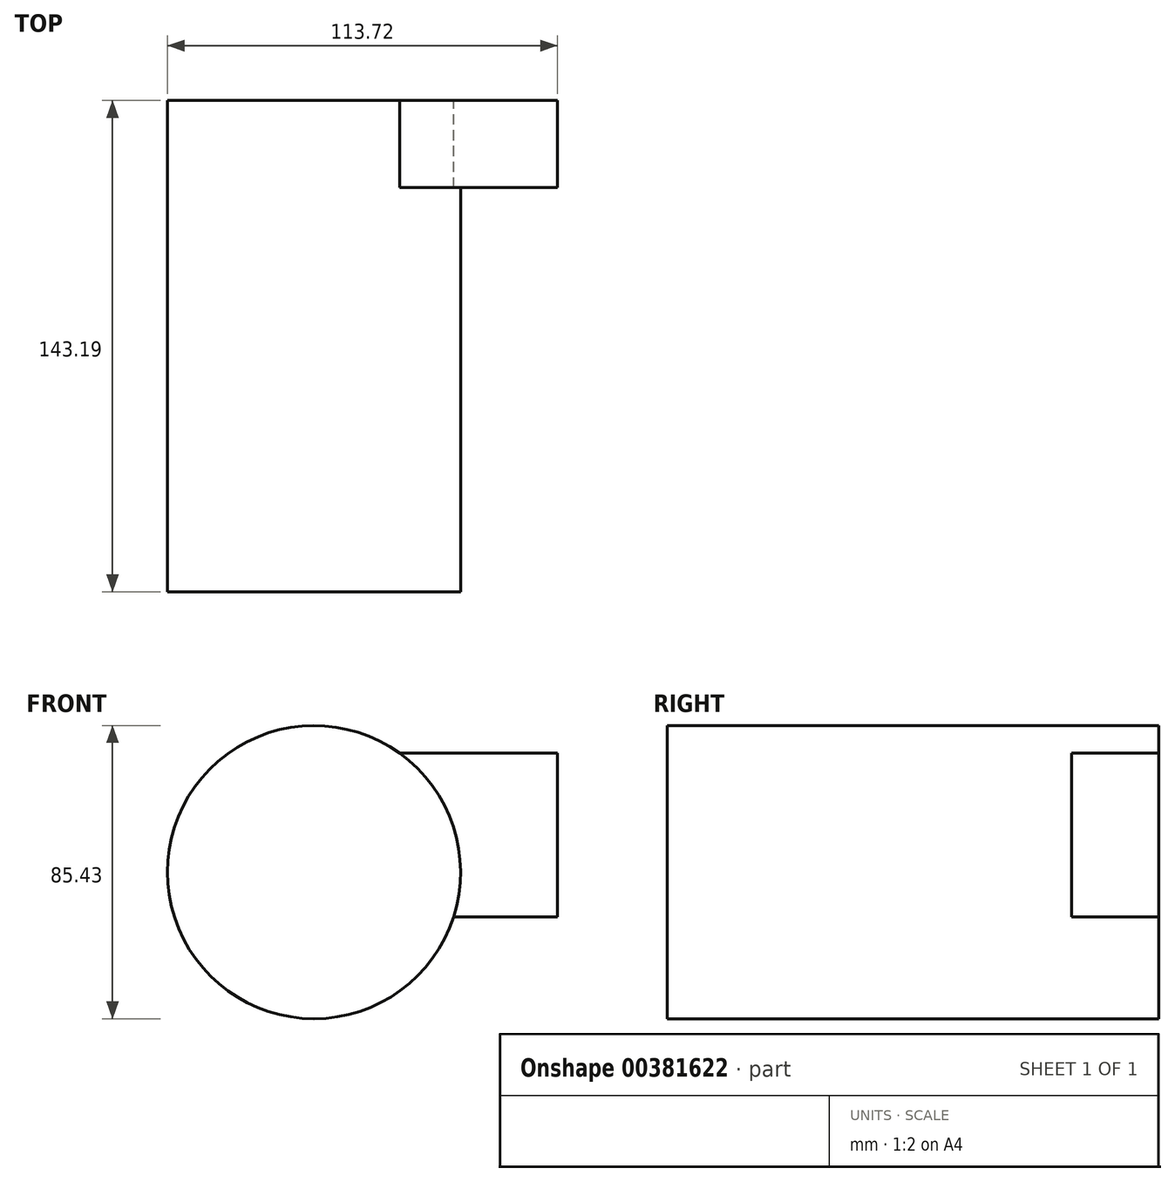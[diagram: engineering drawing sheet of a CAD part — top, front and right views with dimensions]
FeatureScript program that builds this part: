
annotation { "Feature Type Name" : "Feature", "Feature Type Description" : "" }
export const myFeature = defineFeature(function(context is Context, id is Id, definition is map)
    precondition{}
    {
        {
            var Q0;
            Q0=qCreatedBy(makeId("Front.planeOp"),FACE);
            var sketch = newSketch(context, id + "F0", { "sketchPlane" : qUnion([Q0])});
            skCircle(sketch, "E0", {"center": v(6.75, 13.03) * mm, "radius": 42.71 * mm});
            skSolve(sketch);
        }
        {
            var Q0;
            Q0=makeQuery(id+"F0.imprint","IMPRINT",FACE,{"disambiguationData":[TD([[makeQuery(id+"F0.imprint","IMPRINT",EDGE,{"derivedFrom":sQuery(id+"F0.wireOp",EDGE,"E0")}),1.0]])]});
            extrude(context, id + "F1", {"entities" : qUnion([Q0]), "depth" : 67 * mm});
        }
        {
            var Q0;
            Q0=qCreatedBy(makeId("Front.planeOp"),FACE);
            var sketch = newSketch(context, id + "F2", { "sketchPlane" : qUnion([Q0])});
            skLineSegment(sketch, "E1.bottom", {"start": v(52.36, 0) * mm, "end": v(0, 0) * mm});
            skLineSegment(sketch, "E1.top", {"start": v(52.36, 47.73) * mm, "end": v(0, 47.73) * mm});
            skLineSegment(sketch, "E1.left", {"start": v(52.36, 0) * mm, "end": v(52.36, 47.73) * mm});
            skLineSegment(sketch, "E1.right", {"start": v(0, 0) * mm, "end": v(0, 47.73) * mm});
            skSolve(sketch);
        }
        {
            var Q0;
            Q0=makeQuery(id+"F1.opExtrude","CAP_FACE",FACE,{"disambiguationData":[OSD([sQuery(id+"F0.wireOp",EDGE,"E0")])],"isStart":false});
            var Q1;
            Q1=makeQuery(id+"F2.imprint","IMPRINT",FACE,{"disambiguationData":[TD([[makeQuery(id+"F2.imprint","IMPRINT",EDGE,{"derivedFrom":sQuery(id+"F2.wireOp",EDGE,"E1.bottom")}),-1.0]])]});
            extrude(context, id + "F3", {"entities" : qUnion([Q0, Q1]), "operationType" : NewBodyOperationType.ADD, "depth" : 25.4 * mm});
        }
        {
            var Q0;
            Q0=makeQuery(id+"F3.opExtrude","SWEPT_FACE",FACE,{"disambiguationData":[OSD([sQuery(id+"F2.wireOp",EDGE,"E1.left")])]});
            extrude(context, id + "F4", {"entities" : qUnion([Q0]), "operationType" : NewBodyOperationType.ADD, "depth" : 25.4 * mm});
        }
        {
            var Q0;
            Q0=makeQuery(id+"F3.opExtrude","CAP_FACE",FACE,{"disambiguationData":[OSD([sQuery(id+"F0.wireOp",EDGE,"E0")])],"isStart":false});
            extrude(context, id + "F5", {"entities" : qUnion([Q0]), "operationType" : NewBodyOperationType.ADD, "depth" : 25.4 * mm});
        }
        {
            var Q0;
            Q0=makeQuery(id+"F5.opExtrude","CAP_FACE",FACE,{"disambiguationData":[OSD([sQuery(id+"F0.wireOp",EDGE,"E0")])],"isStart":false});
            extrude(context, id + "F6", {"entities" : qUnion([Q0]), "operationType" : NewBodyOperationType.ADD, "depth" : 25.4 * mm});
        }
    });
